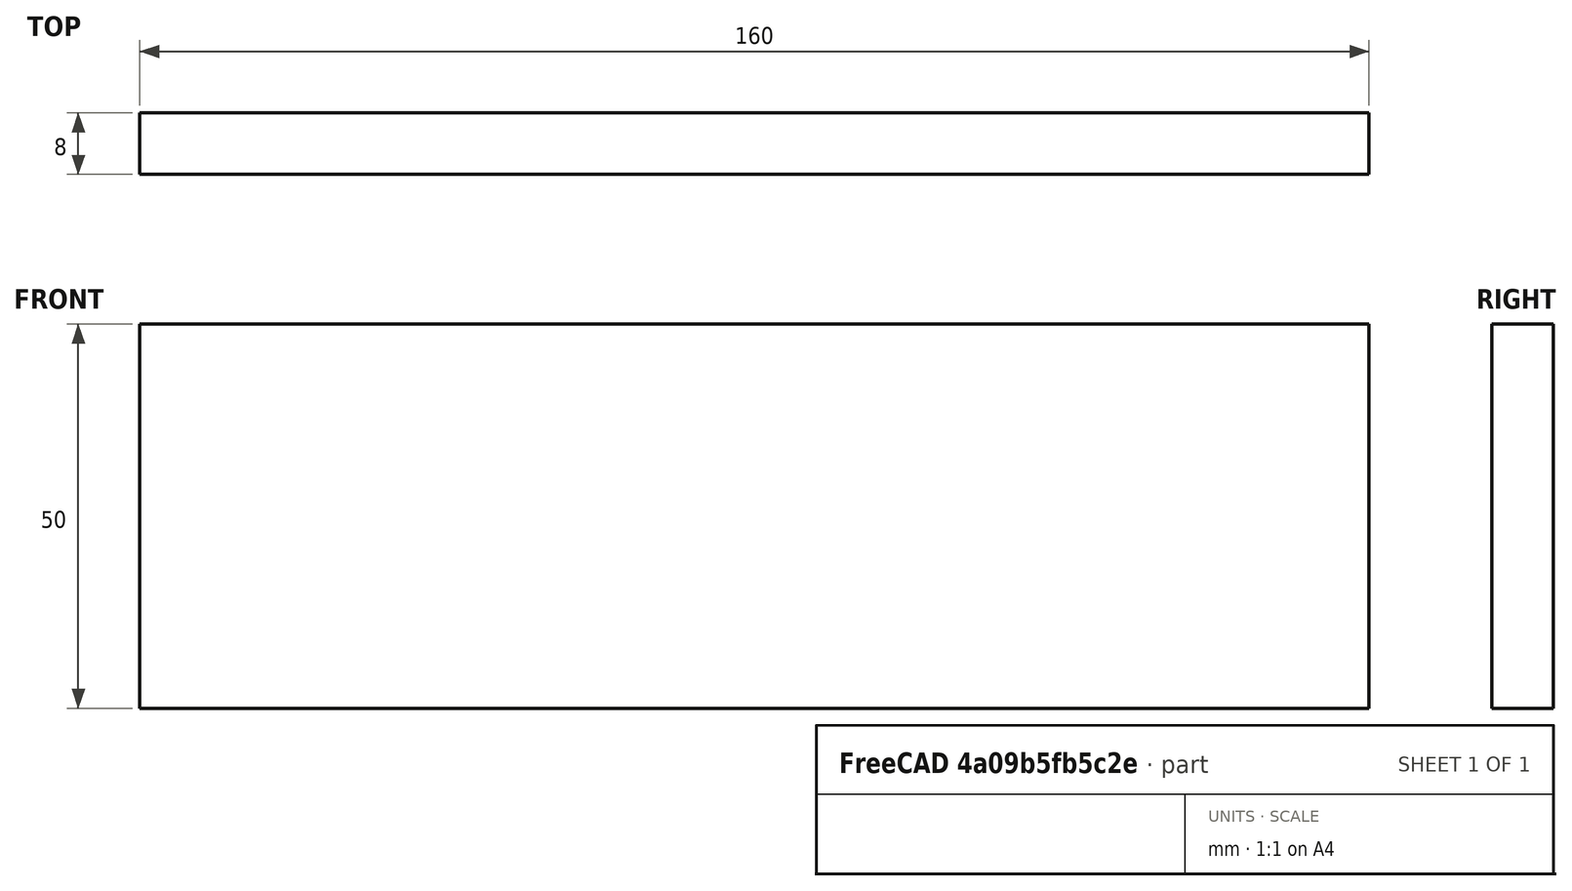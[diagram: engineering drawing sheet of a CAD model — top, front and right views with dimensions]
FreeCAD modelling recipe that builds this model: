
FCSTD DOCUMENT  (FreeCAD 0.15R4671 (Git))
Label: Flat Bar 160x8 EN10058 S235JR
License: All rights reserved
LicenseURL: http://en.wikipedia.org/wiki/All_rights_reserved
objects: Sketcher::SketchObject×1, Part::Extrusion×1
note: 2 computed .brp shape members not serialized (recipe doc carries the construction recipe); baked Part::Feature solids carry a one-line shape summary decoded from their .brp

FEATURE [Sketcher::SketchObject] Sketch
  sketch-geometry (4):
    g0: LineSegment StartX=-80 StartY=-4 StartZ=0 EndX=80 EndY=-4 EndZ=0
    g1: LineSegment StartX=80 StartY=-4 StartZ=0 EndX=80 EndY=4 EndZ=0
    g2: LineSegment StartX=80 StartY=4 StartZ=0 EndX=-80 EndY=4 EndZ=0
    g3: LineSegment StartX=-80 StartY=4 StartZ=0 EndX=-80 EndY=-4 EndZ=0
  constraints (12):
    c: Coincident(g0,g1)
    c: Coincident(g1,g2)
    c: Coincident(g2,g3)
    c: Coincident(g3,g0)
    c: Horizontal(g0)
    c: Horizontal(g2)
    c: Vertical(g1)
    c: Vertical(g3)
    c: Symmetric(g1,g2,g-2)
    c: Symmetric(g0,g1,g-1)
    c: DistanceY(g1) = 8
    c: DistanceX(g0) = 160
FEATURE [Part::Extrusion] Extrude  label="Flat Bar 160x8 EN10058 S235JR"
  Base = -> Sketch
  Dir = (0,0,50)
  Solid = true
